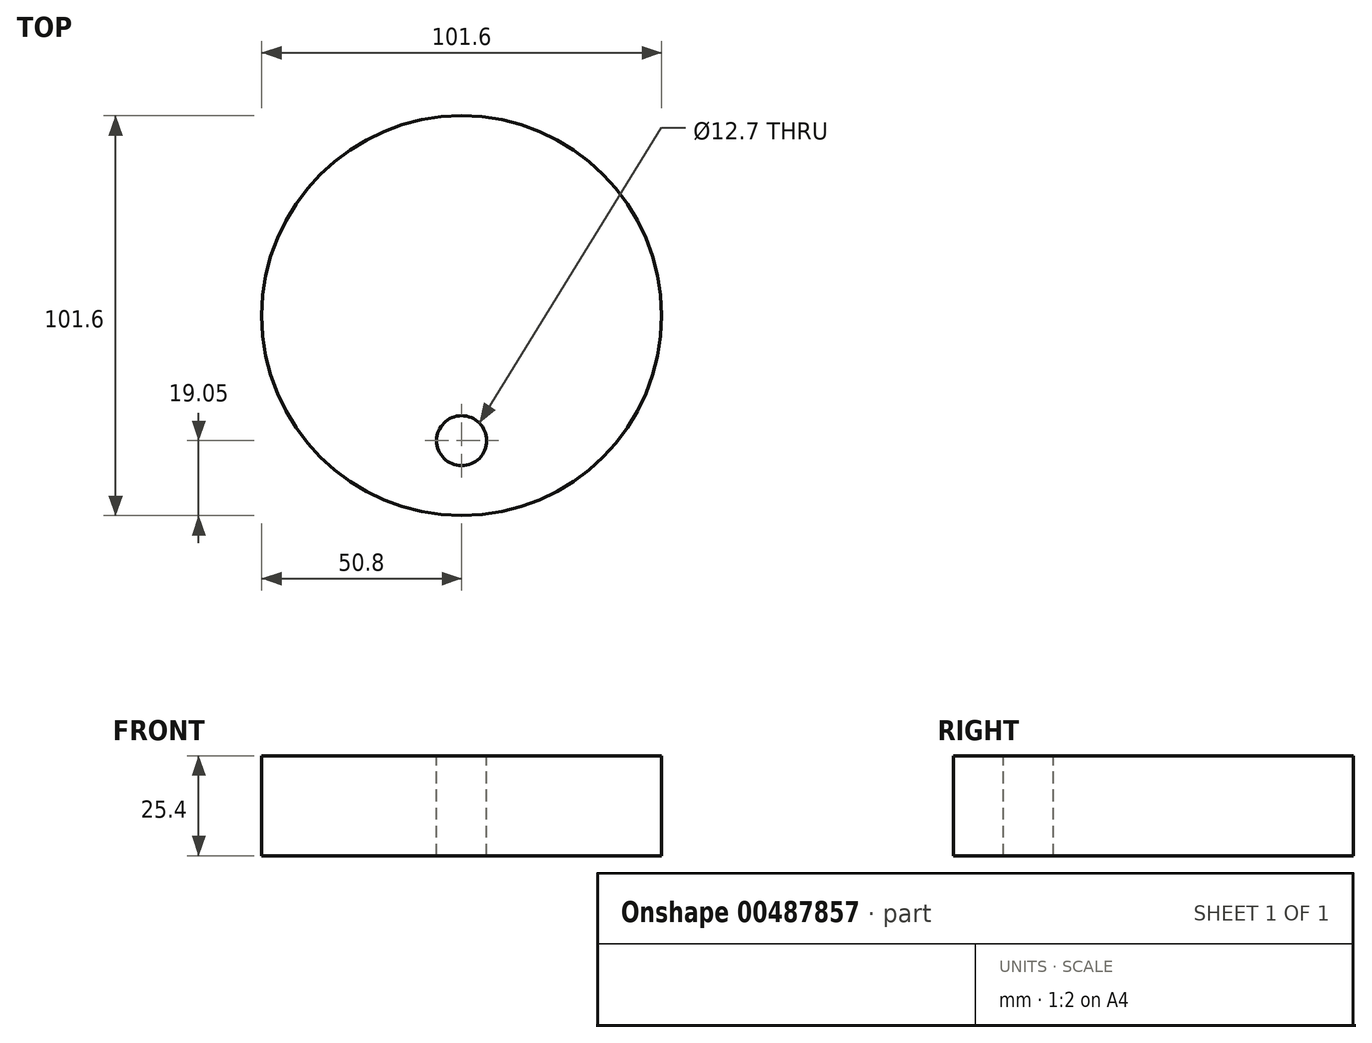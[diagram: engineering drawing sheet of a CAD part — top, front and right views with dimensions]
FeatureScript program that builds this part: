
annotation { "Feature Type Name" : "Feature", "Feature Type Description" : "" }
export const myFeature = defineFeature(function(context is Context, id is Id, definition is map)
    precondition{}
    {
        {
            var Q0;
            Q0=qCreatedBy(makeId("Top.planeOp"),FACE);
            var sketch = newSketch(context, id + "F0", { "sketchPlane" : qUnion([Q0])});
            skCircle(sketch, "E0", {"center": v(0, 0) * mm, "radius": 50.8 * mm});
            skSolve(sketch);
        }
        {
            var Q0;
            Q0 = qSketchRegion(id + "F0", true);
            extrude(context, id + "F1", {"entities" : qUnion([Q0]), "depth" : 25.4 * mm});
        }
        {
            var Q0;
            Q0=makeQuery(id+"F1.opExtrude","CAP_FACE",FACE,{"disambiguationData":[OSD([sQuery(id+"F0.wireOp",EDGE,"E0")])],"isStart":false});
            var sketch = newSketch(context, id + "F2", { "sketchPlane" : qUnion([Q0])});
            skCircle(sketch, "E1", {"center": v(0, 0) * mm, "radius": 31.75 * mm, "construction": true});
            skCircle(sketch, "E2", {"center": v(0, -31.75) * mm, "radius": 6.35 * mm});
            skSolve(sketch);
        }
        {
            var Q0;
            Q0=makeQuery(id+"F1.opExtrude","CAP_FACE",FACE,{"disambiguationData":[OSD([sQuery(id+"F0.wireOp",EDGE,"E0")])],"isStart":false});
            var sketch = newSketch(context, id + "F3", { "sketchPlane" : qUnion([Q0])});
            skCircle(sketch, "E3", {"center": v(0, 0) * mm, "radius": 31.75 * mm, "construction": true});
            skSolve(sketch);
        }
        {
            var Q0;
            Q0 = qSketchRegion(id + "F2", true);
            extrude(context, id + "F4", {"entities" : qUnion([Q0]), "operationType" : NewBodyOperationType.REMOVE, "endBound" : BoundingType.THROUGH_ALL, "oppositeDirection" : true, "depth" : 25.4 * mm});
        }
    });
